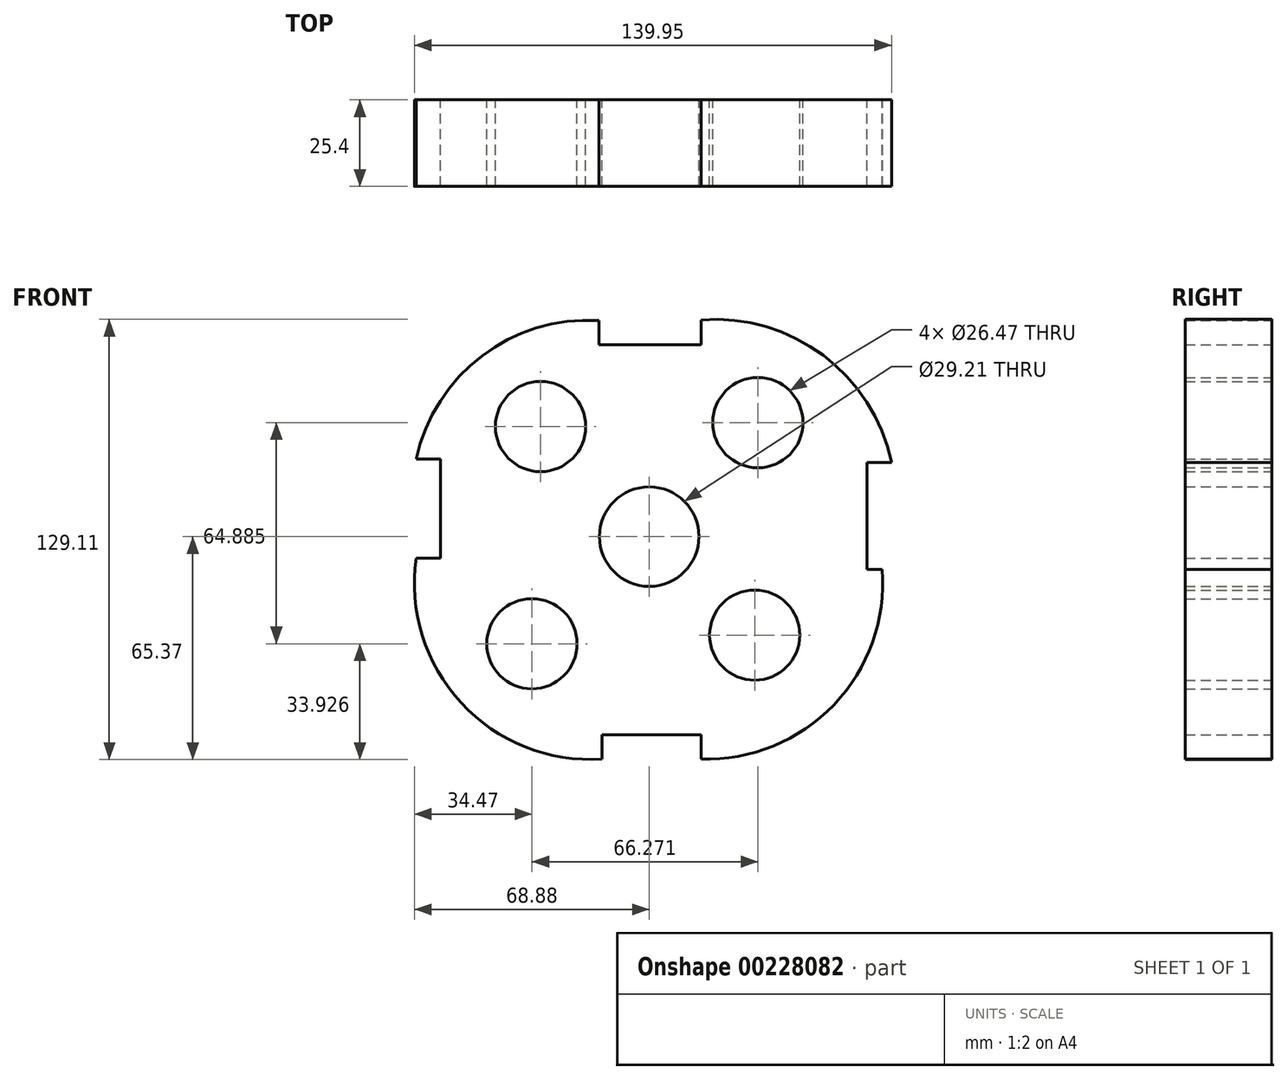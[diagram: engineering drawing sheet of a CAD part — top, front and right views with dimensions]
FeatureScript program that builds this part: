
annotation { "Feature Type Name" : "Feature", "Feature Type Description" : "" }
export const myFeature = defineFeature(function(context is Context, id is Id, definition is map)
    precondition{}
    {
        {
            var Q0;
            Q0=qCreatedBy(makeId("Front.planeOp"),FACE);
            var sketch = newSketch(context, id + "F0", { "sketchPlane" : qUnion([Q0])});
            skCircle(sketch, "E0", {"center": v(0, 0) * mm, "radius": 14.6 * mm});
            skLineSegment(sketch, "E1", {"start": v(-61.2, 22.74) * mm, "end": v(-61.2, -6.35) * mm});
            skLineSegment(sketch, "E2", {"start": v(-61.2, -6.35) * mm, "end": v(-68.35, -6.35) * mm});
            skLineSegment(sketch, "E3", {"start": v(-61.2, 22.74) * mm, "end": v(-68.35, 22.74) * mm});
            skLineSegment(sketch, "E4", {"start": v(-13.9, -58.1) * mm, "end": v(15.2, -58.1) * mm});
            skLineSegment(sketch, "E5", {"start": v(15.2, -58.1) * mm, "end": v(15.2, -65.26) * mm});
            skLineSegment(sketch, "E6", {"start": v(-13.9, -58.1) * mm, "end": v(-13.9, -65.26) * mm});
            skLineSegment(sketch, "E7", {"start": v(-14.78, 56.23) * mm, "end": v(15.2, 56.23) * mm});
            skLineSegment(sketch, "E8", {"start": v(-14.78, 56.23) * mm, "end": v(-14.78, 63.38) * mm});
            skLineSegment(sketch, "E9", {"start": v(15.2, 56.23) * mm, "end": v(15.2, 63.58) * mm});
            skArc(sketch, "E10", {"start": v(-14.78, 63.38) * mm, "mid": v(-49.08, 52.97) * mm, "end": v(-68.35, 22.74) * mm});
            skArc(sketch, "E11", {"start": v(-68.35, -6.35) * mm, "mid": v(-55.15, -48.77) * mm, "end": v(-13.9, -65.26) * mm});
            skLineSegment(sketch, "E12", {"start": v(63.92, 21.8) * mm, "end": v(71.07, 21.8) * mm});
            skArc(sketch, "E13", {"start": v(71.07, 21.8) * mm, "mid": v(51, 53.2) * mm, "end": v(15.2, 63.58) * mm});
            skLineSegment(sketch, "E14", {"start": v(63.92, 21.8) * mm, "end": v(63.92, -9.66) * mm});
            skLineSegment(sketch, "E15", {"start": v(63.92, -9.66) * mm, "end": v(68.33, -9.66) * mm});
            skArc(sketch, "E16", {"start": v(15.2, -65.26) * mm, "mid": v(54.17, -49.32) * mm, "end": v(68.33, -9.66) * mm});
            skCircle(sketch, "E17", {"center": v(-31.87, 32.29) * mm, "radius": 13.23 * mm});
            skCircle(sketch, "E18", {"center": v(-34.41, -31.44) * mm, "radius": 13.23 * mm});
            skCircle(sketch, "E19", {"center": v(30.94, -28.9) * mm, "radius": 13.23 * mm});
            skCircle(sketch, "E20", {"center": v(31.86, 33.44) * mm, "radius": 13.23 * mm});
            skSolve(sketch);
        }
        {
            var Q0;
            Q0 = qSketchRegion(id + "F0", true);
            extrude(context, id + "F1", {"entities" : qUnion([Q0]), "depth" : 25.4 * mm});
        }
    });
